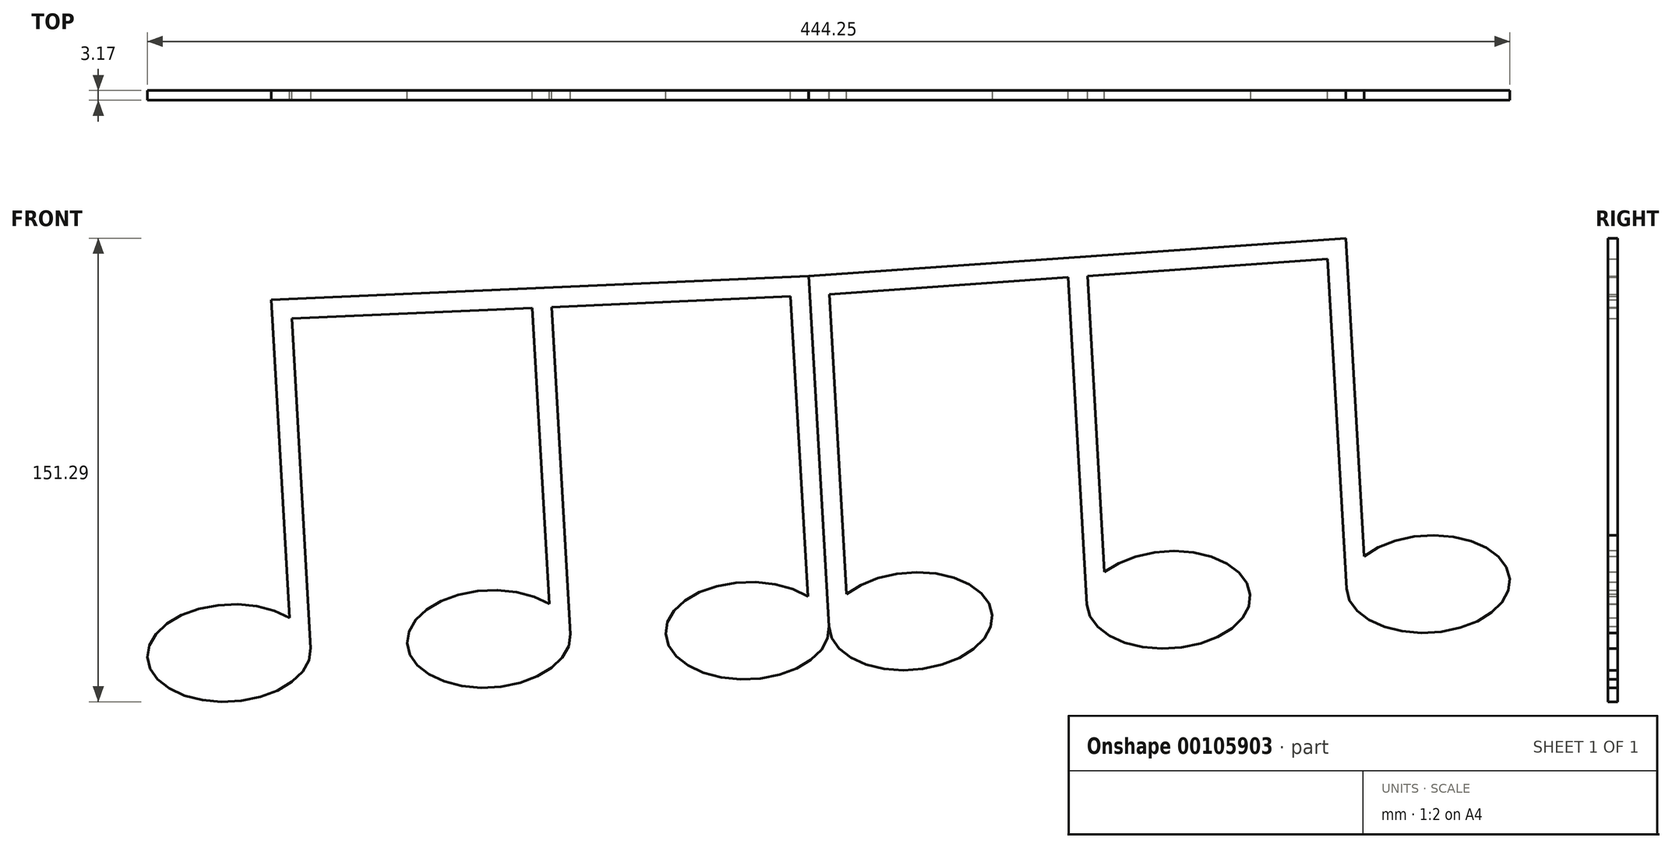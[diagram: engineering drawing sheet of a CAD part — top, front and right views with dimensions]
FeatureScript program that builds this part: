
annotation { "Feature Type Name" : "Feature", "Feature Type Description" : "" }
export const myFeature = defineFeature(function(context is Context, id is Id, definition is map)
    precondition{}
    {
        {
            var Q0;
            Q0=qCreatedBy(makeId("Front.planeOp"),FACE);
            var sketch = newSketch(context, id + "F0", { "sketchPlane" : qUnion([Q0])});
            skEllipticalArc(sketch, "E0", {});
            skLineSegment(sketch, "E1", {"start": v(-96.56, 61.83) * mm, "end": v(-90.58, -41.96) * mm});
            skEllipticalArc(sketch, "E2", {});
            skLineSegment(sketch, "E3", {"start": v(-83.65, -51.86) * mm, "end": v(-89.85, 55.77) * mm});
            skLineSegment(sketch, "E4", {"start": v(-89.85, 55.77) * mm, "end": v(-11.46, 59.22) * mm});
            skLineSegment(sketch, "E5", {"start": v(-11.46, 59.22) * mm, "end": v(-5.9, -37.36) * mm});
            skEllipticalArc(sketch, "E6", {});
            skLineSegment(sketch, "E7", {"start": v(85.38, -45.14) * mm, "end": v(78.79, 69.56) * mm});
            skLineSegment(sketch, "E8", {"start": v(-96.56, 61.83) * mm, "end": v(78.79, 69.56) * mm});
            skLineSegment(sketch, "E9", {"start": v(1.02, -47.26) * mm, "end": v(-5.12, 59.5) * mm});
            skLineSegment(sketch, "E10", {"start": v(78.44, -34.94) * mm, "end": v(72.8, 62.94) * mm});
            skLineSegment(sketch, "E11", {"start": v(-5.12, 59.5) * mm, "end": v(72.8, 62.94) * mm});
            const initialGuessF0  = {"E0": [-0.11027111832196713, -0.05338767367915405, -0.9983503663845338, -0.057415554859873374, 0.02667, 0.015875, 3.8462036373423194, 3.141592653589793], "E2": [-0.02560198107327845, -0.04879003142414705, -0.9983503663845338, -0.057415554859873874, 0.02667, 0.015875, 3.846140072042636, 3.141592653589793], "E6": [0.05873090709330103, -0.04607965118914773, 0.9993844003803591, 0.03508304827676903, 0.02667, 0.015875, 0.7180525695510467, 0.026618218474432444]};
            skSetInitialGuess(sketch, initialGuessF0);
            skSolve(sketch);
        }
        {
            var Q0;
            Q0=qSketchRegion(id+"F0",true);
            extrude(context, id + "F1", {"entities" : qUnion([Q0]), "depth" : 3.17 * mm});
        }
        {
            var Q0;
            Q0=makeQuery(id+"F1.opExtrude","SWEPT_BODY",BODY,{"disambiguationData":[OSD([sQuery(id+"F0.wireOp",EDGE,"E0"),sQuery(id+"F0.wireOp",EDGE,"E1"),sQuery(id+"F0.wireOp",EDGE,"E2"),sQuery(id+"F0.wireOp",EDGE,"E3"),sQuery(id+"F0.wireOp",EDGE,"E4"),sQuery(id+"F0.wireOp",EDGE,"E5"),sQuery(id+"F0.wireOp",EDGE,"E6"),sQuery(id+"F0.wireOp",EDGE,"E7"),sQuery(id+"F0.wireOp",EDGE,"E8"),sQuery(id+"F0.wireOp",EDGE,"E9"),sQuery(id+"F0.wireOp",EDGE,"E10"),sQuery(id+"F0.wireOp",EDGE,"E11")])]});
            var Q1;
            Q1=makeQuery(id+"F1.opExtrude","SWEPT_FACE",FACE,{"disambiguationData":[OSD([sQuery(id+"F0.wireOp",EDGE,"E7")])]});
            mirror(context, id + "F2", {"entities" : qUnion([Q0]), "mirrorPlane" : qUnion([Q1])});
        }
    });
